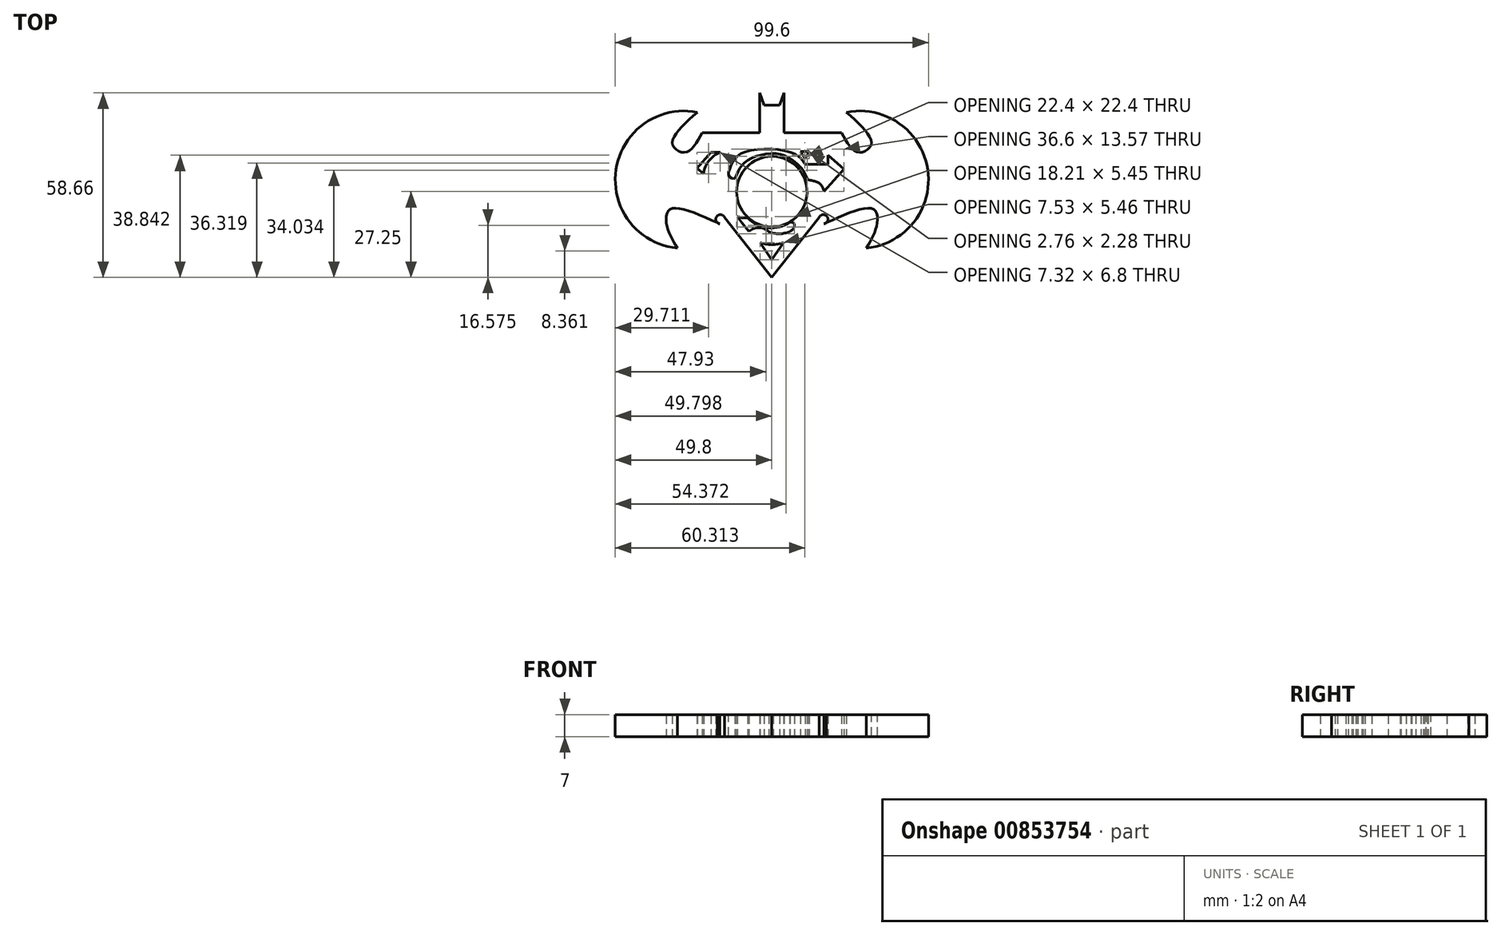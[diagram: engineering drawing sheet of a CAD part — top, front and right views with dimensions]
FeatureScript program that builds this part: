
annotation { "Feature Type Name" : "Feature", "Feature Type Description" : "" }
export const myFeature = defineFeature(function(context is Context, id is Id, definition is map)
    precondition{}
    {
        {
            var Q0;
            Q0=qCreatedBy(makeId("Top.planeOp"),FACE);
            var sketch = newSketch(context, id + "F0", { "sketchPlane" : qUnion([Q0])});
            skArc(sketch, "E0", {"start": v(-0.17, 11.2) * mm, "mid": v(-0.15, -11.2) * mm, "end": v(0.46, 11.2) * mm});
            skLineSegment(sketch, "E1", {"start": v(0, 15.11) * mm, "end": v(20.25, 15.11) * mm});
            skLineSegment(sketch, "E2", {"start": v(20.25, 15.11) * mm, "end": v(26.14, 8.39) * mm});
            skLineSegment(sketch, "E3", {"start": v(26.14, 8.39) * mm, "end": v(0, -24.74) * mm});
            skLineSegment(sketch, "E4.MirrorCS", {"start": v(0, 15.11) * mm, "end": v(-20.25, 15.11) * mm});
            skLineSegment(sketch, "E5.MirrorCS", {"start": v(-26.14, 8.39) * mm, "end": v(0, -24.74) * mm});
            skLineSegment(sketch, "E6.MirrorCS", {"start": v(-20.25, 15.11) * mm, "end": v(-26.14, 8.39) * mm});
            skLineSegment(sketch, "E7", {"start": v(-3.85, 18.68) * mm, "end": v(-3.85, 25.82) * mm});
            skLineSegment(sketch, "E8", {"start": v(-3.85, 25.82) * mm, "end": v(-3.85, 31.41) * mm});
            skLineSegment(sketch, "E9", {"start": v(-3.85, 31.41) * mm, "end": v(-2.5, 27.56) * mm});
            skLineSegment(sketch, "E10", {"start": v(-2.5, 27.56) * mm, "end": v(0, 27.56) * mm});
            skLineSegment(sketch, "E11", {"start": v(-3.85, 18.68) * mm, "end": v(-22.17, 18.68) * mm});
            skFitSpline(sketch, "E12", {"points": [v(-22.17, 18.68) * mm, v(-27.57, 12.51) * mm, v(-31.62, 15.11) * mm, v(-23.71, 25.24) * mm], "startDerivative": vector(-14.43, -26.35) * mm, "endDerivative": vector(30.37, 26.98) * mm});
            skArc(sketch, "E13", {"start": v(-23.71, 25.24) * mm, "mid": v(-49.57, 6.98) * mm, "end": v(-30.08, -17.96) * mm});
            skFitSpline(sketch, "E14", {"points": [v(-30.08, -17.96) * mm, v(-33.36, -10.82) * mm, v(-32.4, -5.62) * mm, v(-16.58, -10.24) * mm], "startDerivative": vector(-13.24, 22.46) * mm, "endDerivative": vector(45.2, -20.63) * mm});
            skArc(sketch, "E15", {"start": v(-15.04, -8.18) * mm, "mid": v(-17.55, -7.9) * mm, "end": v(-16.58, -10.24) * mm});
            skPoint(sketch, "E15.startSnap0", {"position": v(-13.07, -8.18) * mm});
            skLineSegment(sketch, "E16", {"start": v(-15.04, -8.18) * mm, "end": v(0, -27.25) * mm});
            skLineSegment(sketch, "E17.MirrorCS", {"start": v(2.5, 27.56) * mm, "end": v(0, 27.56) * mm});
            skLineSegment(sketch, "E18.MirrorCS", {"start": v(3.85, 31.41) * mm, "end": v(2.5, 27.56) * mm});
            skLineSegment(sketch, "E19.MirrorCS", {"start": v(3.85, 25.82) * mm, "end": v(3.85, 31.41) * mm});
            skLineSegment(sketch, "E20.MirrorCS", {"start": v(3.85, 18.68) * mm, "end": v(22.17, 18.68) * mm});
            skLineSegment(sketch, "E21.MirrorCS", {"start": v(3.85, 18.68) * mm, "end": v(3.85, 25.82) * mm});
            skFitSpline(sketch, "E22.MirrorCS", {"points": [v(22.17, 18.68) * mm, v(27.57, 12.51) * mm, v(31.62, 15.11) * mm, v(23.71, 25.24) * mm], "startDerivative": vector(14.43, -26.35) * mm, "endDerivative": vector(-30.37, 26.98) * mm});
            skArc(sketch, "E23.MirrorCS", {"start": v(23.71, 25.24) * mm, "mid": v(49.57, 6.98) * mm, "end": v(30.08, -17.96) * mm});
            skFitSpline(sketch, "E24.MirrorCS", {"points": [v(30.08, -17.96) * mm, v(33.36, -10.82) * mm, v(32.4, -5.62) * mm, v(16.58, -10.24) * mm], "startDerivative": vector(13.24, 22.46) * mm, "endDerivative": vector(-45.2, -20.63) * mm});
            skArc(sketch, "E25.MirrorCS", {"start": v(15.04, -8.18) * mm, "mid": v(17.55, -7.9) * mm, "end": v(16.58, -10.24) * mm});
            skLineSegment(sketch, "E26.MirrorCS", {"start": v(15.04, -8.18) * mm, "end": v(0, -27.25) * mm});
            skLineSegment(sketch, "E27", {"start": v(-23.75, 7.48) * mm, "end": v(-19.35, 12.47) * mm});
            skLineSegment(sketch, "E28", {"start": v(-19.35, 12.47) * mm, "end": v(-16.43, 12.47) * mm});
            skLineSegment(sketch, "E29", {"start": v(-23.75, 7.48) * mm, "end": v(-21.7, 5.67) * mm});
            skArc(sketch, "E30", {"start": v(-16.43, 12.47) * mm, "mid": v(-20.03, 9.82) * mm, "end": v(-21.7, 5.67) * mm});
            skLineSegment(sketch, "E31", {"start": v(9.13, 12.73) * mm, "end": v(11.9, 12.73) * mm});
            skLineSegment(sketch, "E32", {"start": v(11.9, 12.73) * mm, "end": v(10.62, 10.45) * mm});
            skLineSegment(sketch, "E33", {"start": v(10.62, 10.45) * mm, "end": v(9.13, 12.73) * mm});
            skLineSegment(sketch, "E34", {"start": v(17.83, 11.6) * mm, "end": v(17.83, 8.75) * mm});
            skPoint(sketch, "E34.startSnap0", {"position": v(9.88, 11.6) * mm});
            skLineSegment(sketch, "E35", {"start": v(17.83, 8.75) * mm, "end": v(10.62, 8.75) * mm});
            skLineSegment(sketch, "E36", {"start": v(17.83, 11.6) * mm, "end": v(22.87, 7.22) * mm});
            skLineSegment(sketch, "E37", {"start": v(22.87, 7.22) * mm, "end": v(16.6, 0) * mm});
            skFitSpline(sketch, "E38", {"points": [v(16.6, 0) * mm, v(15.32, 2.46) * mm, v(10.47, 3.97) * mm], "startDerivative": vector(-1.87, 6.47) * mm, "endDerivative": vector(-9.97, 1.71) * mm});
            skPoint(sketch, "E39.3.internal.snap0", {"position": v(-13.01, 18.68) * mm});
            skFitSpline(sketch, "E39", {"points": [v(10.62, 8.75) * mm, v(6.6, 12.29) * mm, v(-8.66, 12.6) * mm, v(-13.01, 8.27) * mm, v(-13.56, 4.8) * mm, v(-10.42, 4.1) * mm], "startDerivative": vector(-14.36, 21.2) * mm, "endDerivative": vector(27.63, -0.31) * mm});
            skLineSegment(sketch, "E40", {"start": v(-3.77, -16.16) * mm, "end": v(0, -21.62) * mm});
            skLineSegment(sketch, "E41.MirrorCS", {"start": v(3.77, -16.16) * mm, "end": v(0, -21.62) * mm});
            skArc(sketch, "E42", {"start": v(-3.77, -16.16) * mm, "mid": v(0, -16.84) * mm, "end": v(3.77, -16.16) * mm});
            skArc(sketch, "E43", {"start": v(-0.97, -12.7) * mm, "mid": v(2.36, -13.4) * mm, "end": v(5.68, -12.67) * mm});
            skArc(sketch, "E44", {"start": v(5.68, -12.67) * mm, "mid": v(6.86, -11.74) * mm, "end": v(7.24, -10.29) * mm});
            skArc(sketch, "E45", {"start": v(7.24, -10.29) * mm, "mid": v(6.24, -9.7) * mm, "end": v(5.11, -9.96) * mm});
            skArc(sketch, "E46", {"start": v(-0.97, -12.7) * mm, "mid": v(-4.1, -11.47) * mm, "end": v(-7.26, -12.67) * mm});
            skLineSegment(sketch, "E47", {"start": v(-7.26, -12.67) * mm, "end": v(-9.42, -9.93) * mm});
            skLineSegment(sketch, "E48", {"start": v(-9.42, -9.93) * mm, "end": v(-10.98, -7.95) * mm});
            skFitSpline(sketch, "E49", {"points": [v(-10.98, -7.95) * mm, v(-9.1, -8.31) * mm, v(-7.49, -8.33) * mm], "startDerivative": vector(3.65, -0.87) * mm, "endDerivative": vector(3.33, 0.14) * mm});
            skLineSegment(sketch, "E50", {"start": v(0, -25.9) * mm, "end": v(8.9, -14.6) * mm});
            skLineSegment(sketch, "E51", {"start": v(8.9, -14.6) * mm, "end": v(21.4, 0.46) * mm});
            skLineSegment(sketch, "E52", {"start": v(21.4, 0.46) * mm, "end": v(27.67, 8.4) * mm});
            skLineSegment(sketch, "E53", {"start": v(27.67, 8.4) * mm, "end": v(20.9, 16.15) * mm});
            skLineSegment(sketch, "E54", {"start": v(20.9, 16.15) * mm, "end": v(-20.36, 16.47) * mm});
            skLineSegment(sketch, "E55", {"start": v(-20.36, 16.47) * mm, "end": v(-27.67, 8.4) * mm});
            skLineSegment(sketch, "E56.MirrorCS", {"start": v(-8.9, -14.6) * mm, "end": v(-21.4, 0.46) * mm});
            skLineSegment(sketch, "E57.MirrorCS", {"start": v(-21.4, 0.46) * mm, "end": v(-27.67, 8.4) * mm});
            skLineSegment(sketch, "E58.MirrorCS", {"start": v(0, -25.9) * mm, "end": v(-8.9, -14.6) * mm});
            skFitSpline(sketch, "E59", {"points": [v(-2.81, -10.84) * mm, v(-2.11, -11) * mm], "startDerivative": vector(0.7, -0.15) * mm, "endDerivative": vector(0.7, -0.15) * mm});
            skLineSegment(sketch, "E60", {"start": v(-0.17, 11.2) * mm, "end": v(0.46, 11.2) * mm});
            skLineSegment(sketch, "E61", {"start": v(-8.1, 7.74) * mm, "end": v(-7.57, 8.25) * mm});
            skLineSegment(sketch, "E62", {"start": v(12.91, 8.75) * mm, "end": v(14.23, 8.75) * mm});
            skLineSegment(sketch, "E63", {"start": v(3.86, -10.51) * mm, "end": v(4.59, -10.22) * mm});
            skFitSpline(sketch, "E64", {"points": [v(-11.76, 4.12) * mm, v(-9.81, 7.97) * mm, v(-6.09, 10.84) * mm, v(1.32, 12.1) * mm, v(6.2, 10.28) * mm, v(9.81, 7) * mm, v(11.37, 3.81) * mm], "startDerivative": vector(10.75, 26.17) * mm, "endDerivative": vector(8.6, -22.95) * mm});
            skArc(sketch, "E65", {"start": v(-7.73, -8.34) * mm, "mid": v(-1.22, -11.51) * mm, "end": v(5.79, -9.7) * mm});
            skSolve(sketch);
        }
        {
            var Q0;
            Q0 = qSketchRegion(id + "F0", true);
            var Q1;
            Q1=makeQuery(id+"F0.imprint","IMPRINT",FACE,{"disambiguationData":[TD([[makeQuery(id+"F0.imprint","IMPRINT",EDGE,{"derivedFrom":sQuery(id+"F0.wireOp",EDGE,"E1")}),-1.0]])]});
            var Q2;
            {var subQ0=sQuery(id+"F0.wireOp",EDGE,"aDcKc5gA-COLU-tZqO-66qd-HIyQaMIgrmTQ");Q2=makeQuery(id+"F0.imprint","IMPRINT",FACE,{"disambiguationData":[TD([[makeQuery(id+"F0.imprint","IMPRINT",EDGE,{"derivedFrom":subQ0}),-1.0]])]});}
            var Q3;
            {var subQ1=sQuery(id+"F0.wireOp",EDGE,"eIsiI6gB-Ll9d-oOkn-LdO6-XLubhWjYAn20");Q3=makeQuery(id+"F0.imprint","IMPRINT",FACE,{"disambiguationData":[TD([[makeQuery(id+"F0.imprint","IMPRINT",EDGE,{"derivedFrom":subQ1}),1.0]])]});}
            var Q4;
            {var subQ3=sQuery(id+"F0.wireOp",EDGE,"6OEurAFr-YUex-DQzQ-EfC9-KjDFJFlvsLat");Q4=makeQuery(id+"F0.imprint","IMPRINT",FACE,{"disambiguationData":[TD([[makeQuery(id+"F0.imprint","IMPRINT",EDGE,{"derivedFrom":subQ3}),-1.0]])]});}
            var Q5;
            {var subQ1=sQuery(id+"F0.wireOp",EDGE,"pgE5huLx-0zxq-FizB-yDCD-FUkinacoNnnC");Q5=makeQuery(id+"F0.imprint","IMPRINT",FACE,{"disambiguationData":[TD([[makeQuery(id+"F0.imprint","IMPRINT",EDGE,{"derivedFrom":subQ1}),-1.0]])]});}
            var Q6;
            {var subQ11=sQuery(id+"F0.wireOp",EDGE,"E65");Q6=makeQuery(id+"F0.imprint","IMPRINT",FACE,{"disambiguationData":[TD([[makeQuery(id+"F0.imprint","IMPRINT",EDGE,{"derivedFrom":subQ11}),1.0]])]});}
            var Q7;
            {var subQ5=sQuery(id+"F0.wireOp",EDGE,"E60");Q7=makeQuery(id+"F0.imprint","IMPRINT",FACE,{"disambiguationData":[TD([[makeQuery(id+"F0.imprint","IMPRINT",EDGE,{"derivedFrom":subQ5}),1.0]])]});}
            extrude(context, id + "F1", {"entities" : qUnion([Q0, Q1, Q2, Q3, Q4, Q5, Q6, Q7]), "depth" : 7 * mm, "offsetDistance" : 25 * mm});
        }
    });
